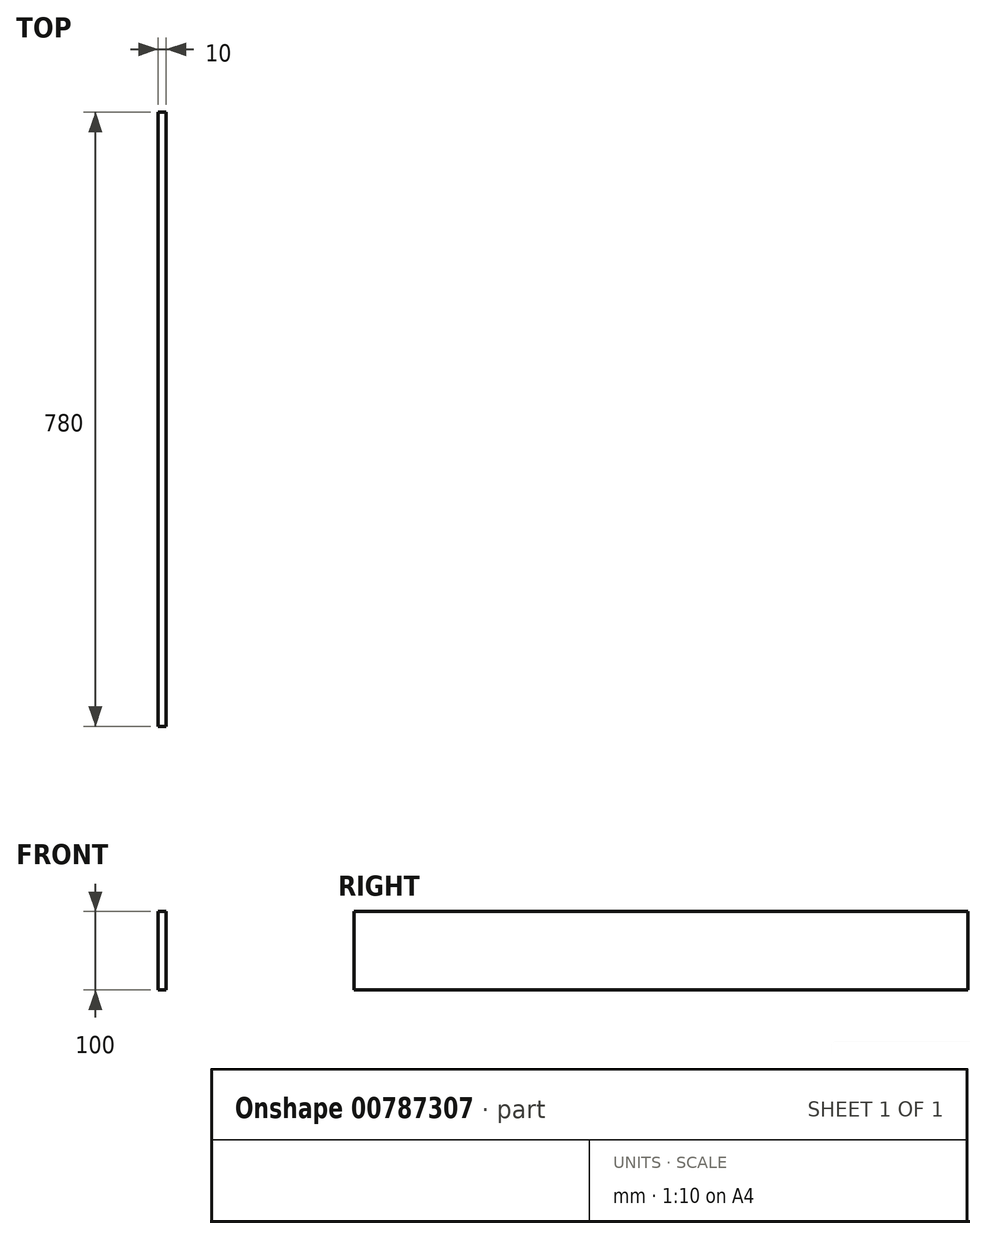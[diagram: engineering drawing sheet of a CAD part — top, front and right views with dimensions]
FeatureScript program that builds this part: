
annotation { "Feature Type Name" : "Feature", "Feature Type Description" : "" }
export const myFeature = defineFeature(function(context is Context, id is Id, definition is map)
    precondition{}
    {
        {
            var Q0;
            Q0=qCreatedBy(makeId("Front.planeOp"),FACE);
            var sketch = newSketch(context, id + "F0", { "sketchPlane" : qUnion([Q0])});
            skLineSegment(sketch, "E0.bottom", {"start": v(5, 50) * mm, "end": v(-5, 50) * mm});
            skLineSegment(sketch, "E0.top", {"start": v(5, -50) * mm, "end": v(-5, -50) * mm});
            skLineSegment(sketch, "E0.left", {"start": v(5, 50) * mm, "end": v(5, -50) * mm});
            skLineSegment(sketch, "E0.right", {"start": v(-5, 50) * mm, "end": v(-5, -50) * mm});
            skPoint(sketch, "E0.middle", {"position": v(0, 0) * mm});
            skSolve(sketch);
        }
        {
            var Q0;
            Q0=makeQuery(id+"F0.imprint","IMPRINT",FACE,{"disambiguationData":[TD([[makeQuery(id+"F0.imprint","IMPRINT",EDGE,{"derivedFrom":sQuery(id+"F0.wireOp",EDGE,"E0.bottom")}),1.0]])]});
            extrude(context, id + "F1", {"entities" : qUnion([Q0]), "depth" : 780 * mm, "offsetDistance" : 25 * mm});
        }
    });
